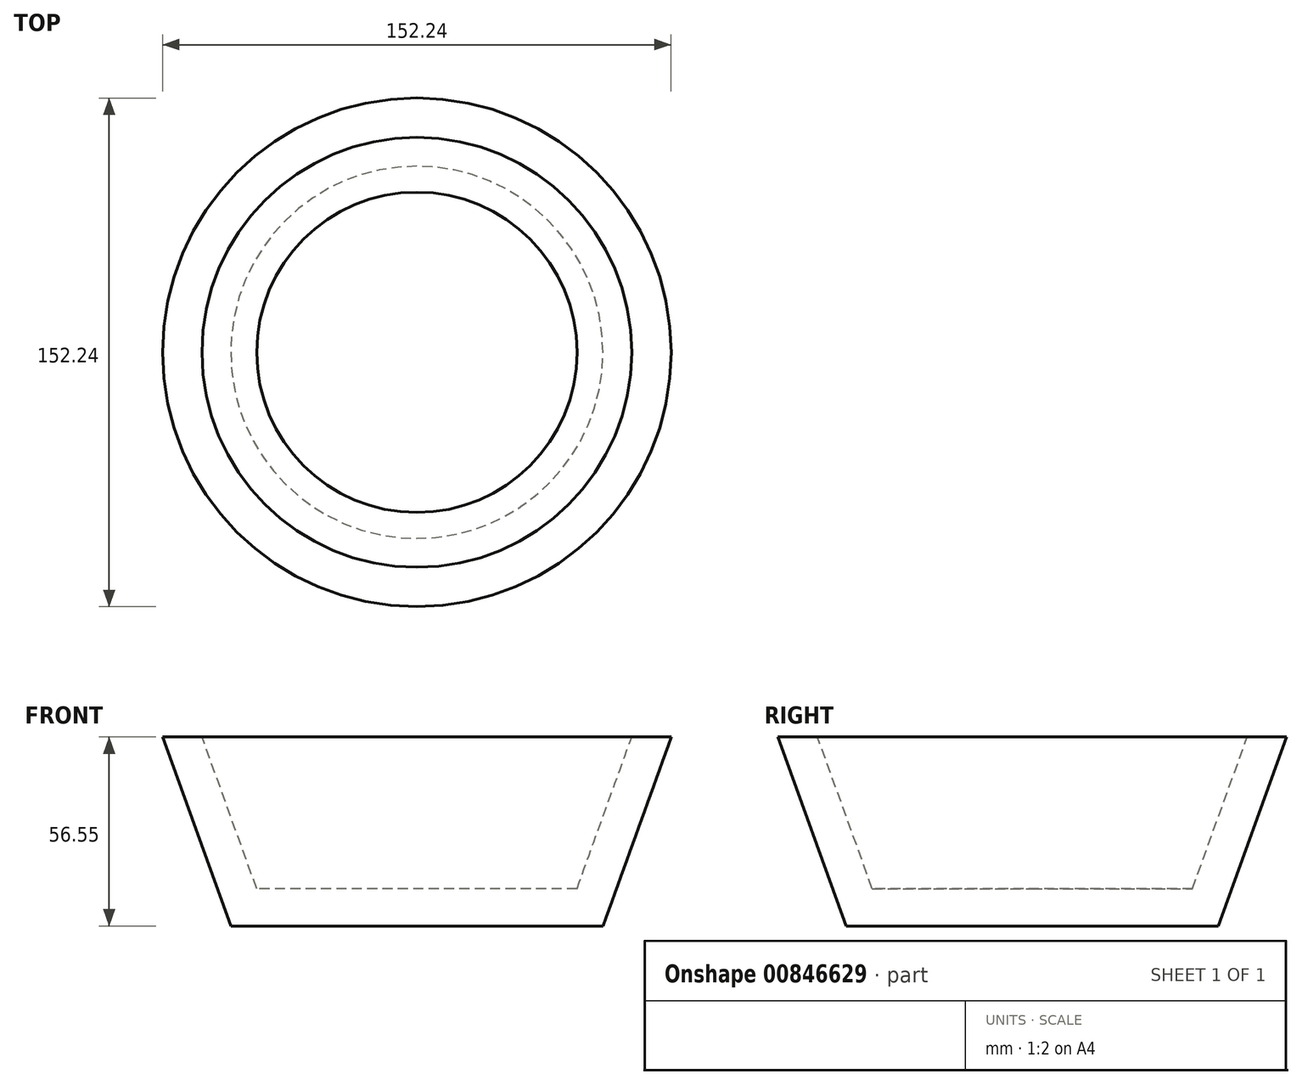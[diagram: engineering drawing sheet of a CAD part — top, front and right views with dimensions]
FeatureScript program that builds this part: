
annotation { "Feature Type Name" : "Feature", "Feature Type Description" : "" }
export const myFeature = defineFeature(function(context is Context, id is Id, definition is map)
    precondition{}
    {
        {
            var Q0;
            Q0=qCreatedBy(makeId("Front.planeOp"),FACE);
            var sketch = newSketch(context, id + "F0", { "sketchPlane" : qUnion([Q0])});
            skLineSegment(sketch, "E0", {"start": v(0, -56.55) * mm, "end": v(55.7, -56.55) * mm});
            skLineSegment(sketch, "E1", {"start": v(55.7, -56.55) * mm, "end": v(76.12, 0) * mm});
            skLineSegment(sketch, "E2", {"start": v(76.12, 0) * mm, "end": v(64.32, 0) * mm});
            skLineSegment(sketch, "E3", {"start": v(64.32, 0) * mm, "end": v(47.93, -45.38) * mm});
            skLineSegment(sketch, "E4", {"start": v(47.93, -45.38) * mm, "end": v(0, -45.38) * mm});
            skLineSegment(sketch, "E5", {"start": v(0, -45.38) * mm, "end": v(0, -56.55) * mm});
            skLineSegment(sketch, "E6", {"start": v(0, 0) * mm, "end": v(0, -65.48) * mm});
            skSolve(sketch);
        }
        {
            var Q0;
            {var subQ0=sQuery(id+"F0.wireOp",EDGE,"E0");Q0=makeQuery(id+"F0.imprint","IMPRINT",FACE,{"disambiguationData":[TD([[makeQuery(id+"F0.imprint","IMPRINT",EDGE,{"derivedFrom":subQ0}),1.0]])]});}
            var Q1;
            Q1=sQuery(id+"F0.wireOp",EDGE,"E5");
            revolve(context, id + "F1", {"surfaceOperationType" : NewSurfaceOperationType.NEW, "entities" : qUnion([Q0]), "axis" : qUnion([Q1]), "revolveType" : RevolveType.FULL});
        }
    });
